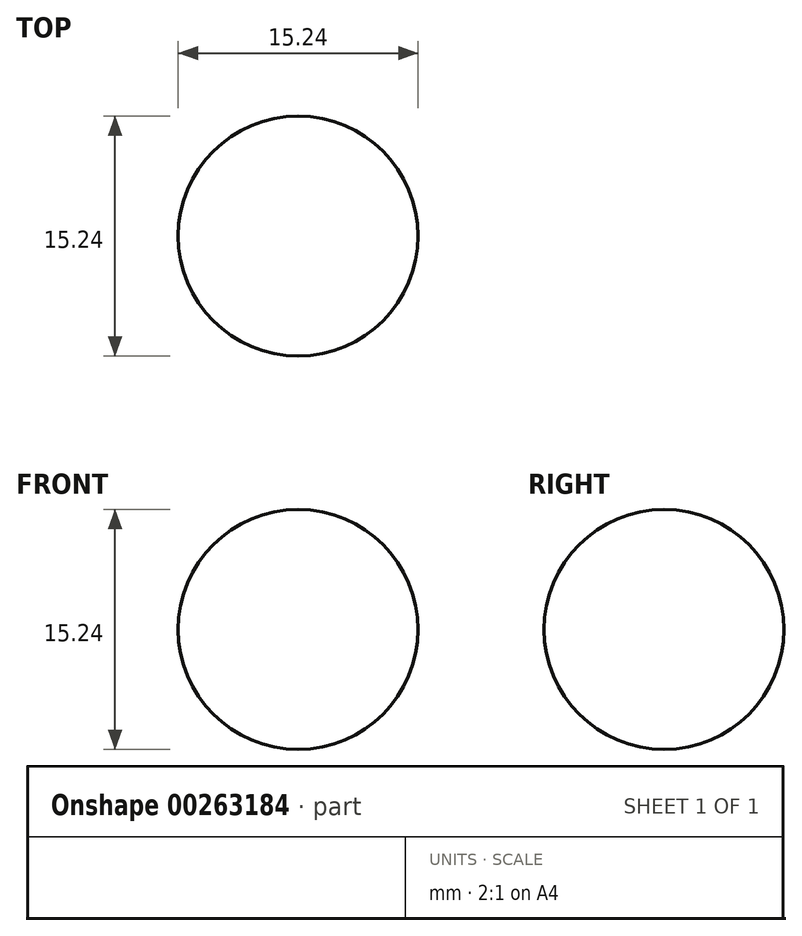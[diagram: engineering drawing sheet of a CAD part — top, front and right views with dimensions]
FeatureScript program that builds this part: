
annotation { "Feature Type Name" : "Feature", "Feature Type Description" : "" }
export const myFeature = defineFeature(function(context is Context, id is Id, definition is map)
    precondition{}
    {
        {
            var Q0;
            Q0=qCreatedBy(makeId("Right.planeOp"),FACE);
            var sketch = newSketch(context, id + "F0", { "sketchPlane" : qUnion([Q0])});
            skArc(sketch, "E0", {"start": v(0, 7.62) * mm, "mid": v(-7.62, 0) * mm, "end": v(0, -7.62) * mm});
            skLineSegment(sketch, "E1", {"start": v(0, 7.62) * mm, "end": v(0, -7.62) * mm});
            skSolve(sketch);
        }
        {
            var Q0;
            Q0=qCreatedBy(makeId("Top.planeOp"),FACE);
            var sketch = newSketch(context, id + "F1", { "sketchPlane" : qUnion([Q0])});
            skCircle(sketch, "E2", {"center": v(0, 0) * mm, "radius": 4.45 * mm});
            skSolve(sketch);
        }
        {
            var Q0;
            Q0=makeQuery(id+"F0.imprint","IMPRINT",FACE,{"disambiguationData":[TD([[makeQuery(id+"F0.imprint","IMPRINT",EDGE,{"derivedFrom":sQuery(id+"F0.wireOp",EDGE,"E0")}),1.0]])]});
            var Q1;
            Q1=sQuery(id+"F1.wireOp",EDGE,"E2");
            revolve(context, id + "F2", {"entities" : qUnion([Q0]), "axis" : qUnion([Q1]), "revolveType" : RevolveType.FULL});
        }
    });
